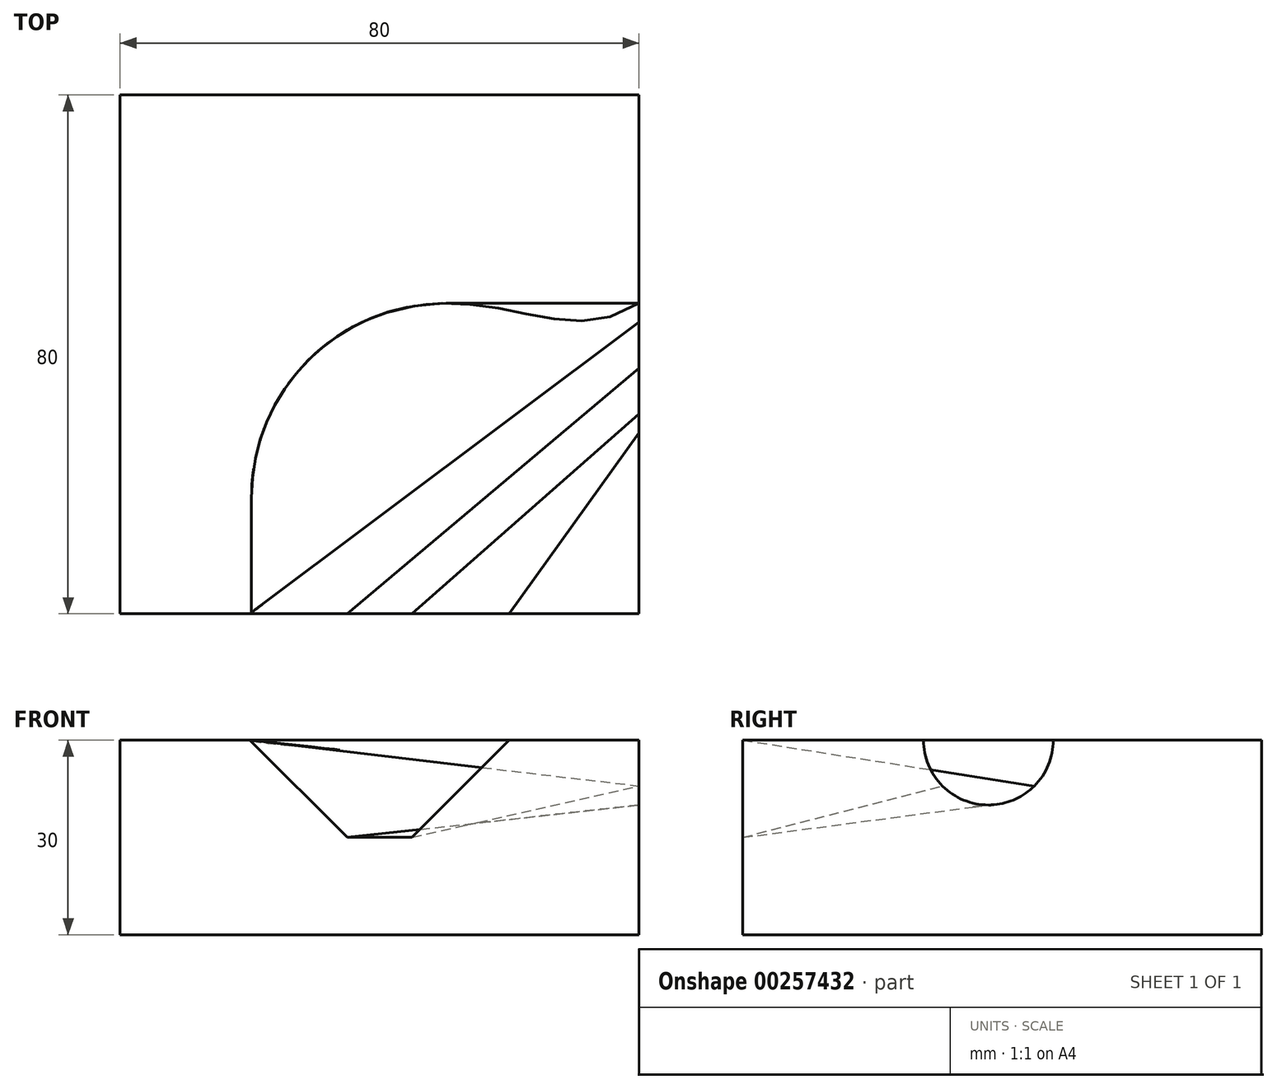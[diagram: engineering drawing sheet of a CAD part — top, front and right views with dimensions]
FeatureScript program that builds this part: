
annotation { "Feature Type Name" : "Feature", "Feature Type Description" : "" }
export const myFeature = defineFeature(function(context is Context, id is Id, definition is map)
    precondition{}
    {
        {
            var Q0;
            Q0=qCreatedBy(makeId("Top.planeOp"),FACE);
            var sketch = newSketch(context, id + "F0", { "sketchPlane" : qUnion([Q0])});
            skLineSegment(sketch, "E0.bottom", {"start": v(40, -40) * mm, "end": v(-40, -40) * mm});
            skLineSegment(sketch, "E0.top", {"start": v(40, 40) * mm, "end": v(-40, 40) * mm});
            skLineSegment(sketch, "E0.left", {"start": v(40, -40) * mm, "end": v(40, 40) * mm});
            skLineSegment(sketch, "E0.right", {"start": v(-40, -40) * mm, "end": v(-40, 40) * mm});
            skPoint(sketch, "E0.middle", {"position": v(0, 0) * mm});
            skSolve(sketch);
        }
        {
            var Q0;
            Q0=makeQuery(id+"F0.imprint","IMPRINT",FACE,{"disambiguationData":[TD([[makeQuery(id+"F0.imprint","IMPRINT",EDGE,{"derivedFrom":sQuery(id+"F0.wireOp",EDGE,"E0.bottom")}),-1.0]])]});
            extrude(context, id + "F1", {"entities" : qUnion([Q0]), "endBound" : BoundingType.SYMMETRIC, "depth" : 30 * mm});
        }
        {
            var Q0;
            Q0=makeQuery(id+"F1.opExtrude","SWEPT_FACE",FACE,{"disambiguationData":[OSD([sQuery(id+"F0.wireOp",EDGE,"E0.bottom")])]});
            var sketch = newSketch(context, id + "F2", { "sketchPlane" : qUnion([Q0])});
            skLineSegment(sketch, "E1.0.0", {"start": v(-40, -15) * mm, "end": v(40, -15) * mm, "construction": true});
            skLineSegment(sketch, "E1.0.1", {"start": v(40, -15) * mm, "end": v(40, 15) * mm, "construction": true});
            skLineSegment(sketch, "E1.0.2", {"start": v(40, 15) * mm, "end": v(-40, 15) * mm, "construction": true});
            skLineSegment(sketch, "E1.0.3", {"start": v(-40, 15) * mm, "end": v(-40, -15) * mm, "construction": true});
            skLineSegment(sketch, "E2", {"start": v(-20, 15) * mm, "end": v(20, 15) * mm});
            skLineSegment(sketch, "E3", {"start": v(20, 15) * mm, "end": v(5, 0) * mm});
            skLineSegment(sketch, "E4", {"start": v(5, 0) * mm, "end": v(-5, 0) * mm});
            skLineSegment(sketch, "E5", {"start": v(-5, 0) * mm, "end": v(-20, 15) * mm});
            skPoint(sketch, "E6", {"position": v(0, 15) * mm});
            skPoint(sketch, "E7", {"position": v(0, 0) * mm});
            skSolve(sketch);
        }
        {
            var Q0;
            Q0=makeQuery(id+"F1.opExtrude","CAP_FACE",FACE,{"disambiguationData":[OSD([sQuery(id+"F0.wireOp",EDGE,"E0.bottom"),sQuery(id+"F0.wireOp",EDGE,"E0.top"),sQuery(id+"F0.wireOp",EDGE,"E0.left"),sQuery(id+"F0.wireOp",EDGE,"E0.right")])],"isStart":false});
            var sketch = newSketch(context, id + "F3", { "sketchPlane" : qUnion([Q0])});
            skLineSegment(sketch, "E8.0.0", {"start": v(40, -40) * mm, "end": v(40, 40) * mm, "construction": true});
            skLineSegment(sketch, "E8.0.1", {"start": v(40, 40) * mm, "end": v(-40, 40) * mm, "construction": true});
            skLineSegment(sketch, "E8.0.2", {"start": v(-40, 40) * mm, "end": v(-40, -40) * mm, "construction": true});
            skLineSegment(sketch, "E8.0.3", {"start": v(-40, -40) * mm, "end": v(40, -40) * mm, "construction": true});
            skArc(sketch, "E9", {"start": v(40, -12.12) * mm, "mid": v(26.86, -23.8) * mm, "end": v(20, -40) * mm});
            skLineSegment(sketch, "E10", {"start": v(-19.76, -40) * mm, "end": v(-19.76, -22.12) * mm});
            skArc(sketch, "E11", {"start": v(10.24, 7.88) * mm, "mid": v(-10.97, -0.91) * mm, "end": v(-19.76, -22.12) * mm});
            skLineSegment(sketch, "E12", {"start": v(10.24, 7.88) * mm, "end": v(40, 7.88) * mm});
            skSolve(sketch);
        }
        {
            var Q0;
            Q0=makeQuery(id+"F1.opExtrude","SWEPT_FACE",FACE,{"disambiguationData":[OSD([sQuery(id+"F0.wireOp",EDGE,"E0.left")])]});
            var sketch = newSketch(context, id + "F4", { "sketchPlane" : qUnion([Q0])});
            skPoint(sketch, "E13.0", {"position": v(-12.12, 15) * mm});
            skPoint(sketch, "E14.0", {"position": v(7.88, 15) * mm});
            skArc(sketch, "E15", {"start": v(-12.12, 15) * mm, "mid": v(-2.12, 5) * mm, "end": v(7.88, 15) * mm});
            skSolve(sketch);
        }
        {
            var Q0;
            {var subQ1=sQuery(id+"F3.wireOp",EDGE,"E9");Q0=makeQuery(id+"F3.imprint","IMPRINT",FACE,{"disambiguationData":[TD([[makeQuery(id+"F3.imprint","IMPRINT",EDGE,{"derivedFrom":subQ1}),-1.0]])]});}
            var sketch = newSketch(context, id + "F5", { "sketchPlane" : qUnion([Q0])});
            skLineSegment(sketch, "E16.0.0", {"start": v(40, 7.88) * mm, "end": v(10.24, 7.88) * mm});
            skArc(sketch, "E16.0.1", {"start": v(10.24, 7.88) * mm, "mid": v(-10.97, -0.91) * mm, "end": v(-19.76, -22.12) * mm});
            skLineSegment(sketch, "E16.0.2", {"start": v(-19.76, -22.12) * mm, "end": v(-19.76, -40) * mm});
            skLineSegment(sketch, "E16.0.3", {"start": v(-19.76, -40) * mm, "end": v(20, -40) * mm, "construction": true});
            skArc(sketch, "E16.0.4", {"start": v(20, -40) * mm, "mid": v(26.86, -23.8) * mm, "end": v(40, -12.12) * mm});
            skLineSegment(sketch, "E16.0.5", {"start": v(40, -12.12) * mm, "end": v(40, 7.88) * mm, "construction": true});
            skSolve(sketch);
        }
        {
            var Q0;
            {var subQ4=sQuery(id+"F3.wireOp",EDGE,"E10");Q0=makeQuery(id+"F3.imprint","IMPRINT",FACE,{"disambiguationData":[TD([[makeQuery(id+"F3.imprint","IMPRINT",EDGE,{"derivedFrom":subQ4}),1.0]])]});}
            var sketch = newSketch(context, id + "F6", { "sketchPlane" : qUnion([Q0])});
            skArc(sketch, "E17.0", {"start": v(10.24, 7.88) * mm, "mid": v(-10.97, -0.91) * mm, "end": v(-19.76, -22.12) * mm});
            skLineSegment(sketch, "E17.1", {"start": v(-19.76, -22.12) * mm, "end": v(-19.76, -40) * mm});
            skLineSegment(sketch, "E17.2", {"start": v(40, 7.88) * mm, "end": v(10.24, 7.88) * mm});
            skArc(sketch, "E18.0", {"start": v(20, -40) * mm, "mid": v(26.86, -23.8) * mm, "end": v(40, -12.12) * mm, "construction": true});
            skSolve(sketch);
        }
        {
            var Q1;
            Q1=makeQuery(id+"F2.imprint","IMPRINT",FACE,{"disambiguationData":[TD([[makeQuery(id+"F2.imprint","IMPRINT",EDGE,{"derivedFrom":sQuery(id+"F2.wireOp",EDGE,"E2")}),1.0]])]});
            var Q2;
            {var subQ0=sQuery(id+"F4.wireOp",EDGE,"E15");Q2=makeQuery(id+"F4.imprint","IMPRINT",FACE,{"disambiguationData":[TD([[makeQuery(id+"F4.imprint","IMPRINT",EDGE,{"derivedFrom":subQ0}),1.0]])]});}
            var Q3;
            Q3 = qConstructionFilter(qBodyType(qCreatedBy(id + "F6" ,EDGE), BodyType.WIRE), ConstructionObject.NO);
            loft(context, id + "F7", {"operationType" : NewBodyOperationType.REMOVE, "addGuides" : true, "sheetProfilesArray" : [{ "sheetProfileEntities" : qUnion([Q1]) }, { "sheetProfileEntities" : qUnion([Q2]) }], "guidesArray" : [{ "guideEntities" : qUnion([Q3]), "guideDerivativeType" : LoftGuideDerivativeType.DEFAULT, "guideDerivativeMagnitude" : 1 }]});
        }
    });
